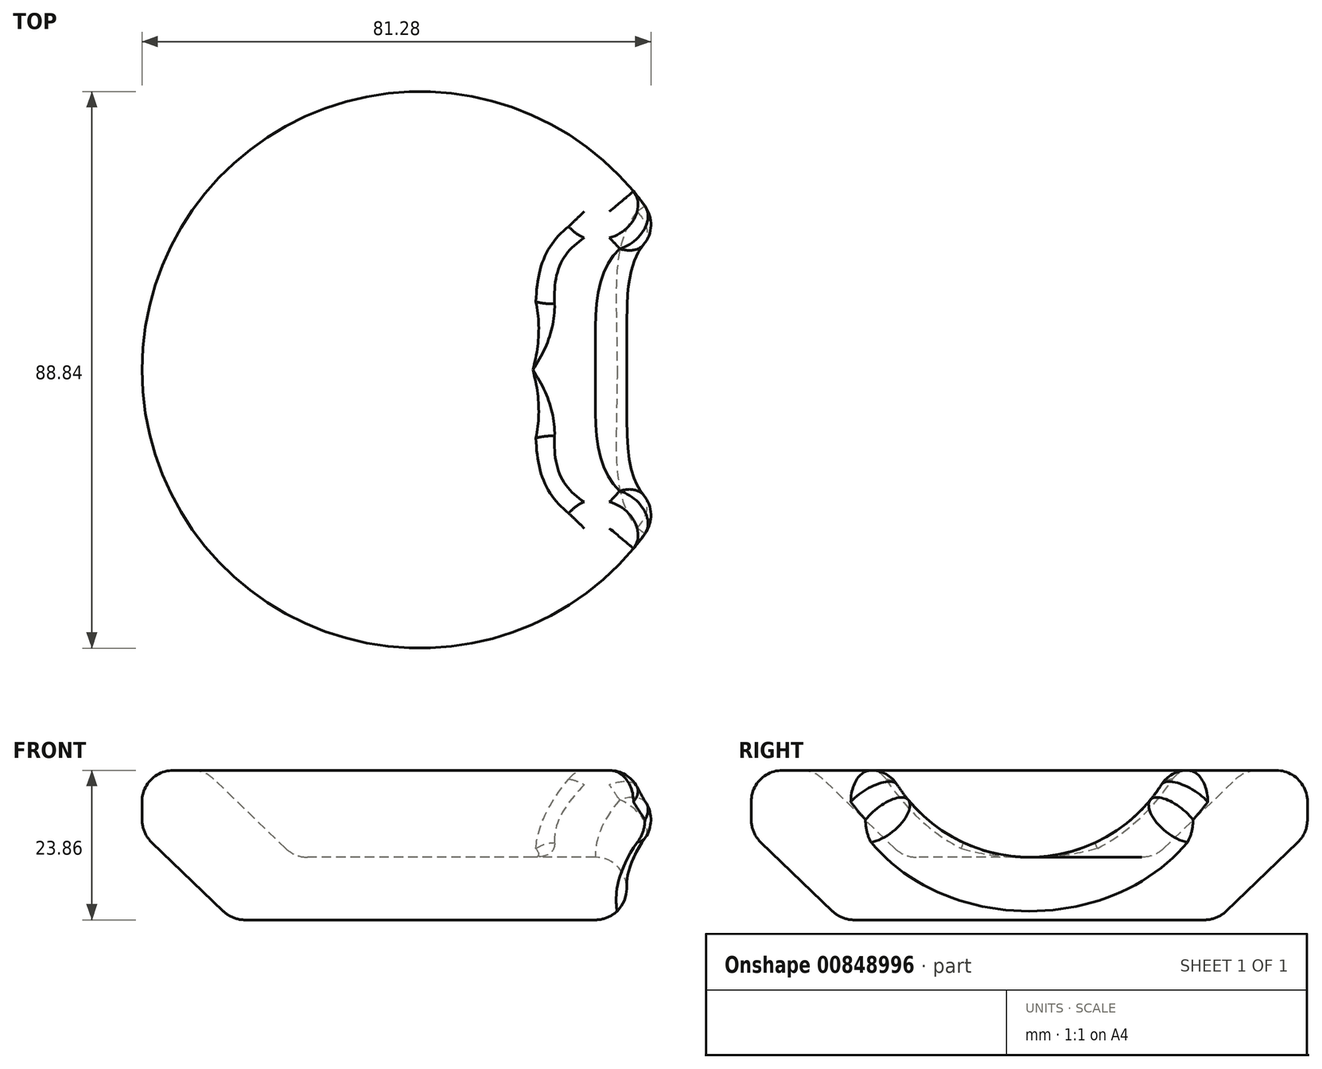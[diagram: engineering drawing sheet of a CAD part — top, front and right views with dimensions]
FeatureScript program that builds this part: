
annotation { "Feature Type Name" : "Feature", "Feature Type Description" : "" }
export const myFeature = defineFeature(function(context is Context, id is Id, definition is map)
    precondition{}
    {
        {
            var Q0;
            Q0=qCreatedBy(makeId("Right.planeOp"),FACE);
            var sketch = newSketch(context, id + "F0", { "sketchPlane" : qUnion([Q0])});
            skLineSegment(sketch, "E0", {"start": v(0, 0) * mm, "end": v(27.99, 0) * mm});
            skLineSegment(sketch, "E1", {"start": v(31.45, 1.4) * mm, "end": v(42.88, 12.39) * mm});
            skLineSegment(sketch, "E2", {"start": v(44.42, 16) * mm, "end": v(44.42, 18.86) * mm});
            skLineSegment(sketch, "E3", {"start": v(39.42, 23.86) * mm, "end": v(36.43, 23.86) * mm});
            skLineSegment(sketch, "E4", {"start": v(32.96, 22.47) * mm, "end": v(21.45, 11.4) * mm});
            skLineSegment(sketch, "E5", {"start": v(17.99, 10) * mm, "end": v(0, 10) * mm});
            skLineSegment(sketch, "E6", {"start": v(0, 10) * mm, "end": v(0, 0) * mm});
            skPoint(sketch, "E7.visualSharp", {"position": v(20, 10) * mm});
            skArc(sketch, "E7.filletArc", {"start": v(17.99, 10) * mm, "mid": v(19.85, 10.36) * mm, "end": v(21.45, 11.4) * mm});
            skPoint(sketch, "E8.visualSharp", {"position": v(30, 0) * mm});
            skArc(sketch, "E8.filletArc", {"start": v(27.99, 0) * mm, "mid": v(29.85, 0.36) * mm, "end": v(31.45, 1.4) * mm});
            skPoint(sketch, "E9.visualSharp", {"position": v(44.42, 13.86) * mm});
            skArc(sketch, "E9.filletArc", {"start": v(42.88, 12.39) * mm, "mid": v(44.02, 14.03) * mm, "end": v(44.42, 16) * mm});
            skPoint(sketch, "E10.visualSharp", {"position": v(34.42, 23.86) * mm});
            skArc(sketch, "E10.filletArc", {"start": v(36.43, 23.86) * mm, "mid": v(34.56, 23.5) * mm, "end": v(32.96, 22.47) * mm});
            skPoint(sketch, "E11.visualSharp", {"position": v(44.42, 23.86) * mm});
            skArc(sketch, "E11.filletArc", {"start": v(44.42, 18.86) * mm, "mid": v(42.95, 22.4) * mm, "end": v(39.42, 23.86) * mm});
            skSolve(sketch);
        }
        {
            var Q0;
            Q0=makeQuery(id+"F0.imprint","IMPRINT",FACE,{"disambiguationData":[TD([[makeQuery(id+"F0.imprint","IMPRINT",EDGE,{"derivedFrom":sQuery(id+"F0.wireOp",EDGE,"E0")}),1.0]])]});
            var Q1;
            Q1=sQuery(id+"F0.wireOp",EDGE,"E6");
            revolve(context, id + "F1", {"surfaceOperationType" : NewSurfaceOperationType.NEW, "entities" : qUnion([Q0]), "axis" : qUnion([Q1]), "revolveType" : RevolveType.FULL});
        }
        {
            var Q0;
            Q0=qCreatedBy(makeId("Right.planeOp"),FACE);
            var sketch = newSketch(context, id + "F2", { "sketchPlane" : qUnion([Q0])});
            skCircle(sketch, "E12", {"center": v(0, 35) * mm, "radius": 25 * mm});
            skSolve(sketch);
        }
        {
            var Q0;
            Q0=makeQuery(id+"F2.imprint","IMPRINT",FACE,{"disambiguationData":[TD([[makeQuery(id+"F2.imprint","IMPRINT",EDGE,{"derivedFrom":sQuery(id+"F2.wireOp",EDGE,"E12")}),1.0]])]});
            extrude(context, id + "F3", {"entities" : qUnion([Q0]), "operationType" : NewBodyOperationType.REMOVE, "depth" : 250 * mm, "offsetDistance" : 25 * mm});
        }
        {
            var Q0;
            Q0=makeQuery(id+"F3.boolean.opBoolean","COPY",FACE,{"derivedFrom":makeQuery(id+"F3.opExtrude","SWEPT_FACE",FACE,{"disambiguationData":[OSD([sQuery(id+"F2.wireOp",EDGE,"E12")])]})});
            fillet(context, id + "F4", {"entities" : qUnion([Q0]), "radius" : 5 * mm, "tangentPropagation" : true, "allowEdgeOverflow" : false});
        }
    });
